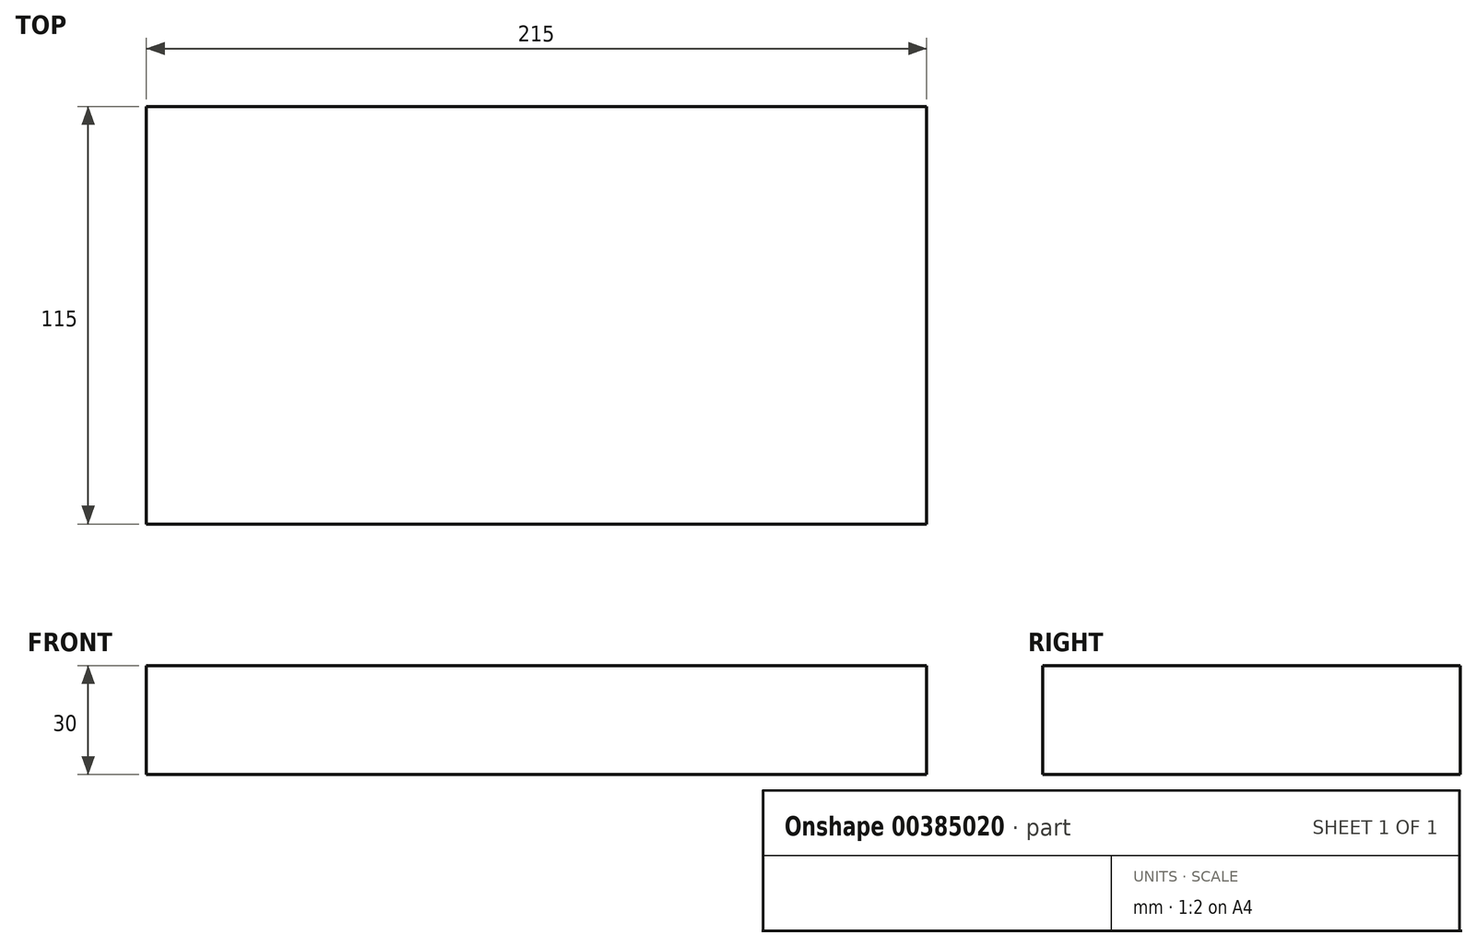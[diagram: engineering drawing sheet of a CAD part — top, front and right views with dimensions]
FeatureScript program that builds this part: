
annotation { "Feature Type Name" : "Feature", "Feature Type Description" : "" }
export const myFeature = defineFeature(function(context is Context, id is Id, definition is map)
    precondition{}
    {
        {
            var Q0;
            Q0=qCreatedBy(makeId("Top.planeOp"),FACE);
            var sketch = newSketch(context, id + "F0", { "sketchPlane" : qUnion([Q0])});
            skLineSegment(sketch, "E0.bottom", {"start": v(0, 0) * mm, "end": v(215, 0) * mm});
            skLineSegment(sketch, "E0.top", {"start": v(0, 115) * mm, "end": v(215, 115) * mm});
            skLineSegment(sketch, "E0.left", {"start": v(0, 0) * mm, "end": v(0, 115) * mm});
            skLineSegment(sketch, "E0.right", {"start": v(215, 0) * mm, "end": v(215, 115) * mm});
            skSolve(sketch);
        }
        {
            var Q0;
            Q0=makeQuery(id+"F0.imprint","IMPRINT",FACE,{"disambiguationData":[TD([[makeQuery(id+"F0.imprint","IMPRINT",EDGE,{"derivedFrom":sQuery(id+"F0.wireOp",EDGE,"E0.bottom")}),1.0]])]});
            extrude(context, id + "F1", {"entities" : qUnion([Q0]), "depth" : 30 * mm});
        }
    });
